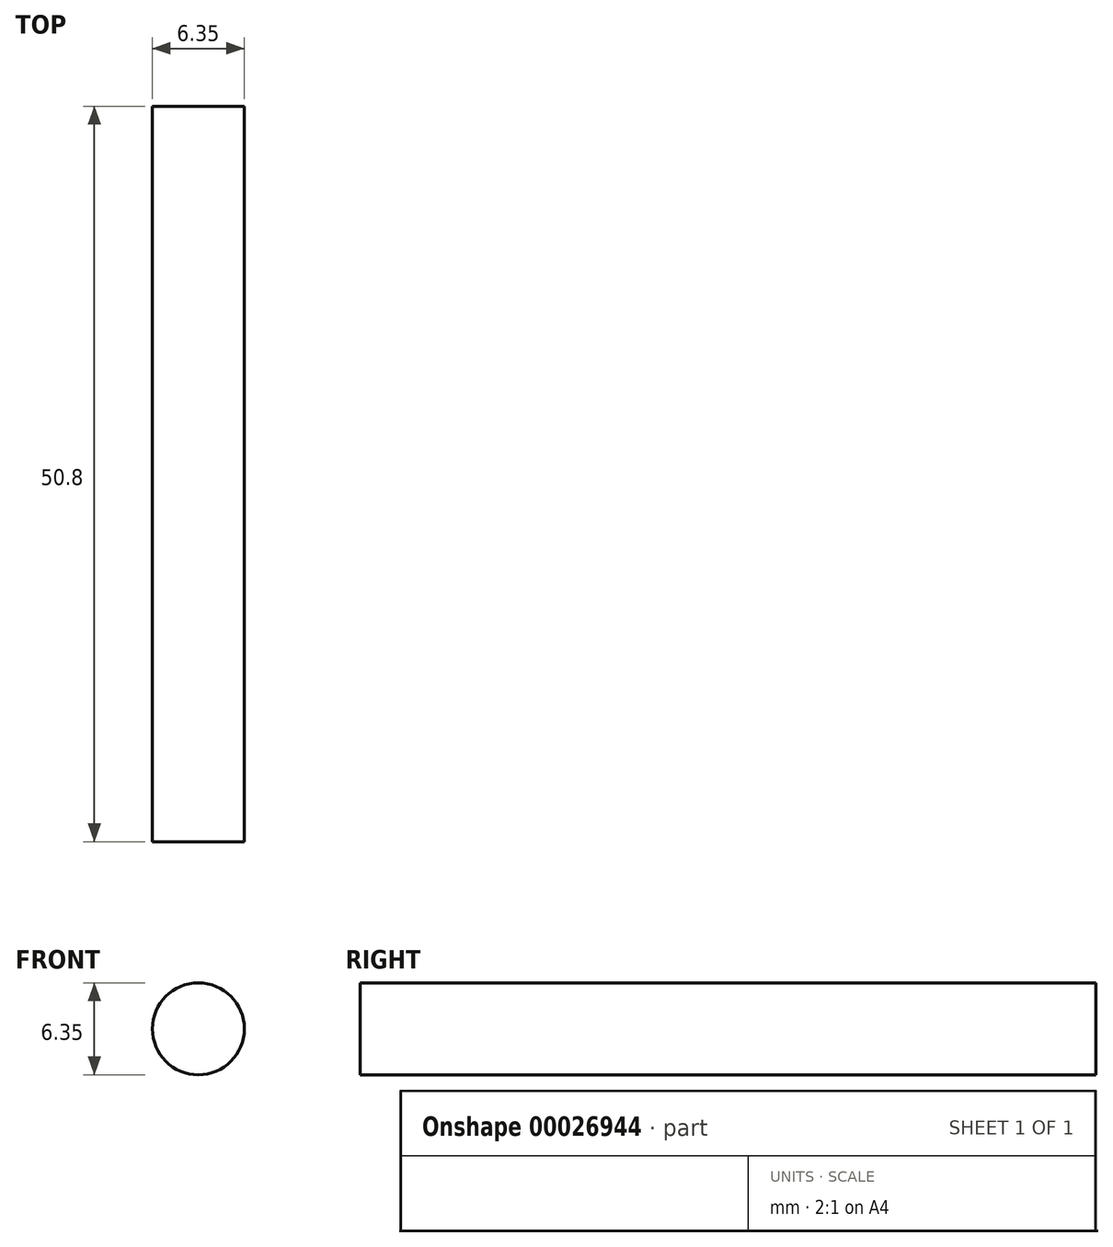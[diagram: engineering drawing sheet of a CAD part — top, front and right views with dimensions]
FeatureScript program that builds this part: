
annotation { "Feature Type Name" : "Feature", "Feature Type Description" : "" }
export const myFeature = defineFeature(function(context is Context, id is Id, definition is map)
    precondition{}
    {
        {
            var Q0;
            Q0=qCreatedBy(makeId("Front.planeOp"),FACE);
            var sketch = newSketch(context, id + "F0", { "sketchPlane" : qUnion([Q0])});
            skCircle(sketch, "E0", {"center": v(-17.98, 4.77) * mm, "radius": 3.18 * mm});
            skSolve(sketch);
        }
        {
            var Q0;
            Q0=makeQuery(id+"F0.imprint","IMPRINT",FACE,{"disambiguationData":[TD([[makeQuery(id+"F0.imprint","IMPRINT",EDGE,{"derivedFrom":sQuery(id+"F0.wireOp",EDGE,"E0")}),1.0]])]});
            extrude(context, id + "F1", {"entities" : qUnion([Q0]), "depth" : 50.8 * mm});
        }
    });
